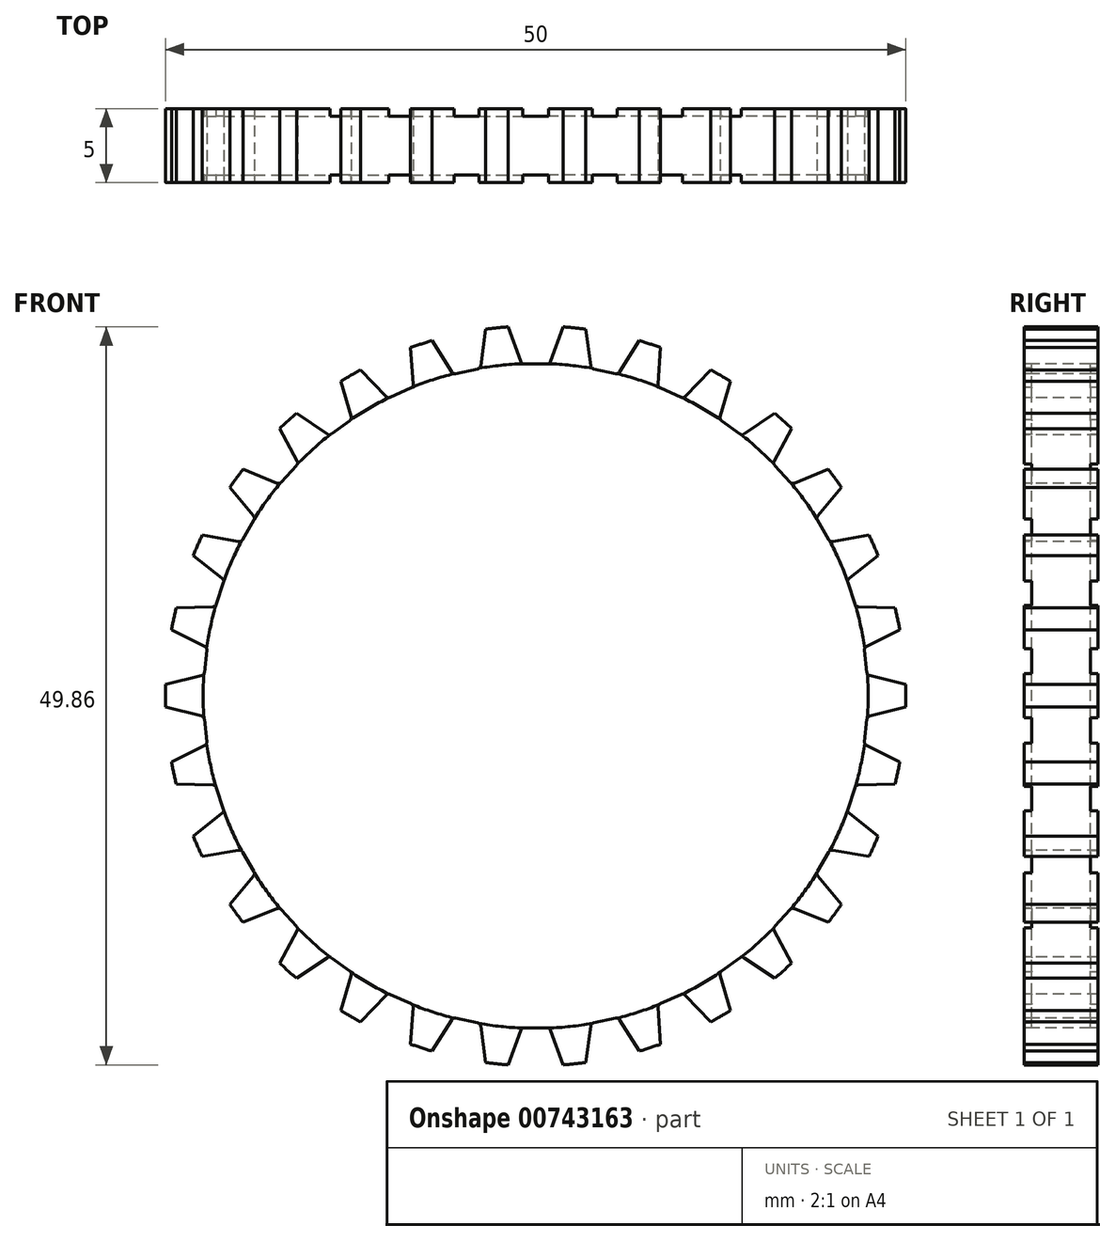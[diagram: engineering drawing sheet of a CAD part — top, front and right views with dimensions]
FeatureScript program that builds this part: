
annotation { "Feature Type Name" : "Feature", "Feature Type Description" : "" }
export const myFeature = defineFeature(function(context is Context, id is Id, definition is map)
    precondition{}
    {
        {
            var Q0;
            Q0=qCreatedBy(makeId("Right.planeOp"),FACE);
            var sketch = newSketch(context, id + "F0", { "sketchPlane" : qUnion([Q0])});
            skLineSegment(sketch, "E0.bottom", {"start": v(2.5, 25) * mm, "end": v(-2.5, 25) * mm});
            skLineSegment(sketch, "E0.top", {"start": v(2.5, -25) * mm, "end": v(-2.5, -25) * mm});
            skPoint(sketch, "E0.middle", {"position": v(0, 0) * mm});
            skLineSegment(sketch, "E1", {"start": v(-2.5, 0) * mm, "end": v(2.5, 0) * mm});
            skLineSegment(sketch, "E2", {"start": v(2, 22.46) * mm, "end": v(2, -22.46) * mm});
            skLineSegment(sketch, "E3", {"start": v(-2, -22.46) * mm, "end": v(-2, 22.46) * mm});
            skLineSegment(sketch, "E4", {"start": v(-2.5, 22.46) * mm, "end": v(-2.5, 25) * mm});
            skLineSegment(sketch, "E5", {"start": v(2.5, 22.46) * mm, "end": v(2.5, 25) * mm});
            skLineSegment(sketch, "E6", {"start": v(2.5, -25) * mm, "end": v(2.5, -22.46) * mm});
            skLineSegment(sketch, "E7", {"start": v(-2.5, -25) * mm, "end": v(-2.5, -22.46) * mm});
            skLineSegment(sketch, "E8", {"start": v(2.5, -22.46) * mm, "end": v(2, -22.46) * mm});
            skLineSegment(sketch, "E9", {"start": v(-2.5, -22.46) * mm, "end": v(-2, -22.46) * mm});
            skLineSegment(sketch, "E10", {"start": v(2.5, 22.46) * mm, "end": v(2, 22.46) * mm});
            skLineSegment(sketch, "E11", {"start": v(-2, 22.46) * mm, "end": v(-2.5, 22.46) * mm});
            skSolve(sketch);
        }
        {
            var Q0;
            Q0=makeQuery(id+"F0.imprint","IMPRINT",FACE,{"disambiguationData":[TD([[makeQuery(id+"F0.imprint","IMPRINT",EDGE,{"derivedFrom":sQuery(id+"F0.wireOp",EDGE,"E0.bottom")}),1.0]])]});
            var Q1;
            Q1=sQuery(id+"F0.wireOp",EDGE,"E1");
            revolve(context, id + "F1", {"surfaceOperationType" : NewSurfaceOperationType.NEW, "entities" : qUnion([Q0]), "axis" : qUnion([Q1]), "revolveType" : RevolveType.FULL});
        }
        {
            var Q0;
            Q0=qCreatedBy(makeId("Front.planeOp"),FACE);
            var sketch = newSketch(context, id + "F2", { "sketchPlane" : qUnion([Q0])});
            skLineSegment(sketch, "E12", {"start": v(-1.83, 24.88) * mm, "end": v(-1, 22.6) * mm});
            skLineSegment(sketch, "E13.MirrorCS", {"start": v(1.83, 24.88) * mm, "end": v(1, 22.6) * mm});
            skLineSegment(sketch, "E14", {"start": v(0.77, 22.43) * mm, "end": v(-0.77, 22.43) * mm});
            skPoint(sketch, "E15.visualSharp", {"position": v(0.94, 22.43) * mm});
            skArc(sketch, "E15.filletArc", {"start": v(0.77, 22.43) * mm, "mid": v(0.91, 22.47) * mm, "end": v(1, 22.6) * mm});
            skPoint(sketch, "E16.visualSharp", {"position": v(-0.94, 22.43) * mm});
            skArc(sketch, "E16.filletArc", {"start": v(-1, 22.6) * mm, "mid": v(-0.91, 22.47) * mm, "end": v(-0.77, 22.43) * mm});
            skLineSegment(sketch, "E17", {"start": v(1.83, 24.88) * mm, "end": v(1.86, 24.95) * mm});
            skLineSegment(sketch, "E18", {"start": v(-1.83, 24.88) * mm, "end": v(-1.86, 24.96) * mm});
            skArc(sketch, "E19", {"start": v(1.86, 24.95) * mm, "mid": v(0, 25.06) * mm, "end": v(-1.86, 24.96) * mm});
            skSolve(sketch);
        }
        {
            var Q0;
            Q0 = qSketchRegion(id + "F2", true);
            extrude(context, id + "F3", {"entities" : qUnion([Q0]), "operationType" : NewBodyOperationType.REMOVE, "endBound" : BoundingType.SYMMETRIC, "oppositeDirection" : true, "depth" : 5 * mm, "offsetDistance" : 25.4 * mm});
        }
        {
            var Q0;
            Q0=makeQuery(id+"F3.boolean.opBoolean","COPY",FACE,{"derivedFrom":makeQuery(id+"F3.opExtrude","SWEPT_FACE",FACE,{"disambiguationData":[OSD([sQuery(id+"F2.wireOp",EDGE,"E12"),sQuery(id+"F2.wireOp",EDGE,"E18")])]})});
            var Q1;
            Q1=makeQuery(id+"F3.boolean.opBoolean","COPY",FACE,{"derivedFrom":makeQuery(id+"F3.opExtrude","SWEPT_FACE",FACE,{"disambiguationData":[OSD([sQuery(id+"F2.wireOp",EDGE,"E14")])]})});
            var Q2;
            Q2=makeQuery(id+"F3.boolean.opBoolean","COPY",FACE,{"derivedFrom":makeQuery(id+"F3.opExtrude","SWEPT_FACE",FACE,{"disambiguationData":[OSD([sQuery(id+"F2.wireOp",EDGE,"E16.filletArc")])]})});
            var Q3;
            Q3=makeQuery(id+"F3.boolean.opBoolean","COPY",FACE,{"derivedFrom":makeQuery(id+"F3.opExtrude","SWEPT_FACE",FACE,{"disambiguationData":[OSD([sQuery(id+"F2.wireOp",EDGE,"E15.filletArc")])]})});
            var Q4;
            Q4=makeQuery(id+"F3.boolean.opBoolean","COPY",FACE,{"derivedFrom":makeQuery(id+"F3.opExtrude","SWEPT_FACE",FACE,{"disambiguationData":[OSD([sQuery(id+"F2.wireOp",EDGE,"E13.MirrorCS"),sQuery(id+"F2.wireOp",EDGE,"E17")])]})});
            var Q5;
            Q5=makeQuery(id+"F1.opRevolve","SWEPT_FACE",FACE,{"disambiguationData":[OSD([sQuery(id+"F0.wireOp",EDGE,"E0.bottom")])]});
            circularPattern(context, id + "F4", {"patternType" : PatternType.FACE, "operationType" : NewBodyOperationType.REMOVE, "faces" : qUnion([Q0, Q1, Q2, Q3, Q4]), "axis" : qUnion([Q5]), "angle" : 360 * degree, "instanceCount" : 30, "equalSpace" : true, "isCentered" : true});
        }
    });
